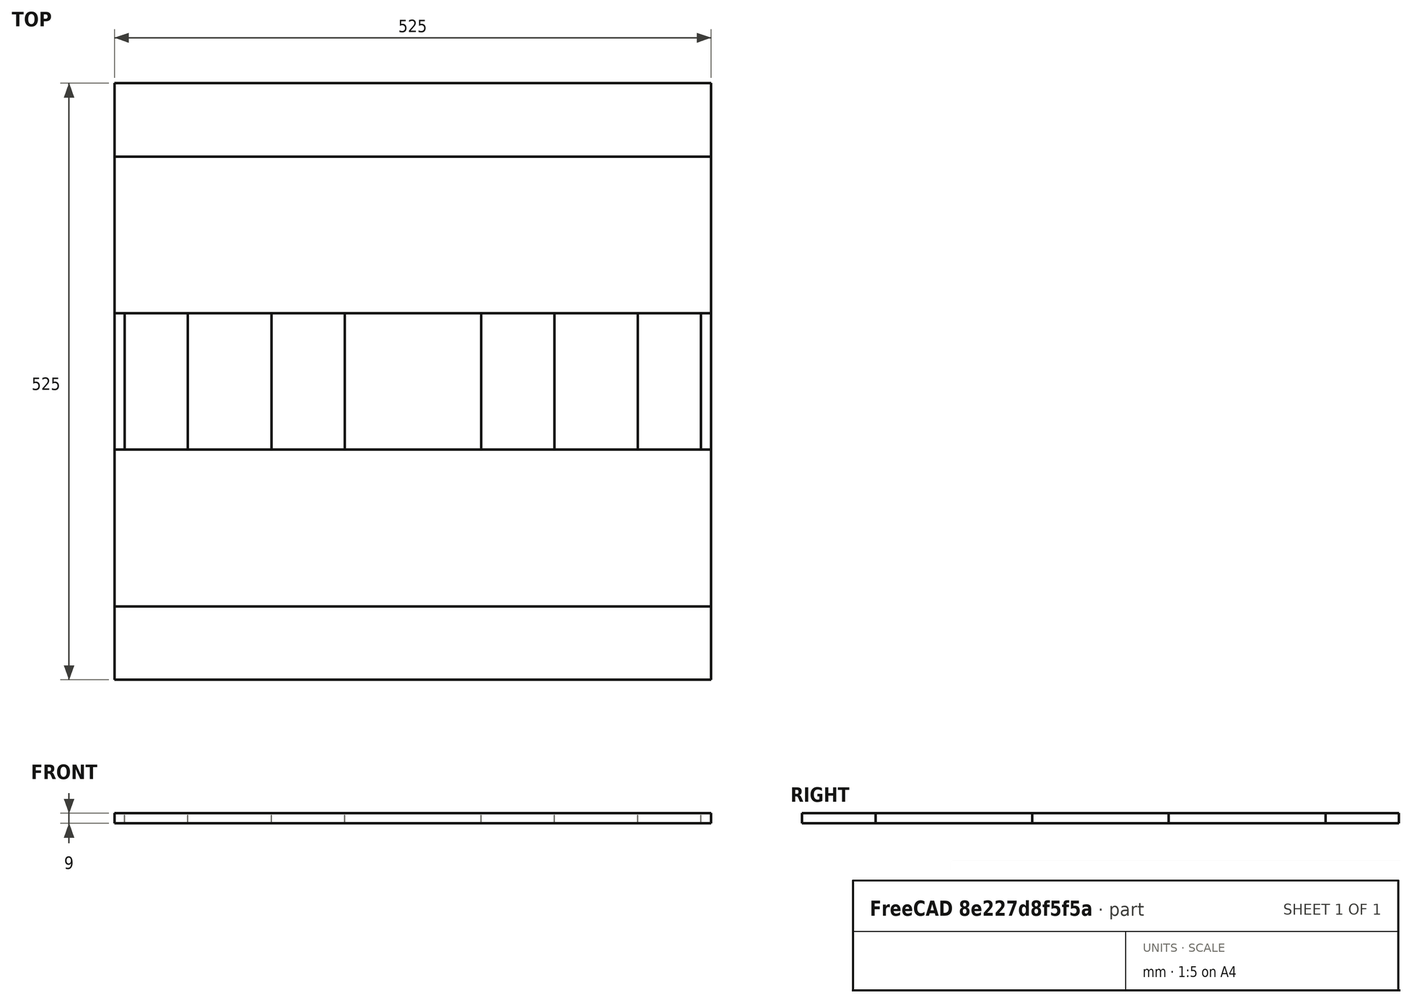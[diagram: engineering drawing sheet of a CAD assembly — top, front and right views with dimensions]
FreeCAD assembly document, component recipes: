
FREECAD ASSEMBLY — COMPONENT RECIPES ("storage-matrix")

This assembly document has 7 components, labeled P0..P6 below (a component is one placed body or linked part). 7 of them carry a construction recipe — the FreeCAD feature program that regenerates the part from scratch, quoted from this document or its linked companion documents; the rest are supplied as boundary geometry only. No exploded tour is included for this assembly.
COMPONENT P0 — recipe-attached ("BackMedium", modeled in this document).
Construction recipe (the document's own serialized feature program — sketch geometry with constraints, then the solid features built on it; lengths are millimeters unless a unit is written):

FEATURE [Sketcher::SketchObject] Sketch007
  MapMode = 5
  Support = -> [XY_Plane007]
  expr: Constraints[11] = Constraints[9] / 2
  expr: Constraints[10] = Constraints[8] / 2
  sketch-geometry (4):
    g0: LineSegment StartX=-262.5 StartY=-198 StartZ=0 EndX=262.5 EndY=-198 EndZ=0
    g1: LineSegment StartX=262.5 StartY=-198 StartZ=0 EndX=262.5 EndY=198 EndZ=0
    g2: LineSegment StartX=262.5 StartY=198 StartZ=0 EndX=-262.5 EndY=198 EndZ=0
    g3: LineSegment StartX=-262.5 StartY=198 StartZ=0 EndX=-262.5 EndY=-198 EndZ=0
  constraints (12):
    c: Coincident(g0,g1)
    c: Coincident(g1,g2)
    c: Coincident(g2,g3)
    c: Coincident(g3,g0)
    c: Horizontal(g0)
    c: Horizontal(g2)
    c: Vertical(g1)
    c: Vertical(g3)
    c: Distance(g2) = 525
    c: Distance(g1) = 396
    c: Distance(g2,g-2) = 262.5
    c: Distance(g1,g-1) = 198
FEATURE [PartDesign::Pad] Pad006
  Direction = (1,1,1)
  Length = 9
  Length2 = 100
  Profile = -> Sketch007
  Type = 0
FEATURE [PartDesign::CoordinateSystem] bottom004
  AttacherType = Attacher::AttachEngine3D
  MapMode = 5
  Placement = pos=(0,-198,0) rot=(1,0,0;1.5708rad)
  Support = -> [Pad006]
FEATURE [PartDesign::Body] BackMedium
  Group = -> [Sketch007,Pad006,bottom004]
  Origin = -> Origin007
  Tip = -> Pad006
COMPONENT P1 — recipe-attached ("back003", modeled in this document).
Construction recipe (the document's own serialized feature program — sketch geometry with constraints, then the solid features built on it; lengths are millimeters unless a unit is written):

FEATURE [PartDesign::CoordinateSystem] LCS_0002
  AttacherType = Attacher::AttachEngine3D
  MapMode = 2
  Support = -> [X_Axis005]
FEATURE [Sketcher::SketchObject] Sketch005
  MapMode = 5
  Support = -> [XY_Plane005]
  expr: Constraints[10] = Constraints[8] / 2
  expr: Constraints[11] = Constraints[9] / 2
  sketch-geometry (4):
    g0: LineSegment StartX=-262.5 StartY=-262.5 StartZ=0 EndX=262.5 EndY=-262.5 EndZ=0
    g1: LineSegment StartX=262.5 StartY=-262.5 StartZ=0 EndX=262.5 EndY=262.5 EndZ=0
    g2: LineSegment StartX=262.5 StartY=262.5 StartZ=0 EndX=-262.5 EndY=262.5 EndZ=0
    g3: LineSegment StartX=-262.5 StartY=262.5 StartZ=0 EndX=-262.5 EndY=-262.5 EndZ=0
  constraints (12):
    c: Coincident(g0,g1)
    c: Coincident(g1,g2)
    c: Coincident(g2,g3)
    c: Coincident(g3,g0)
    c: Horizontal(g0)
    c: Horizontal(g2)
    c: Vertical(g1)
    c: Vertical(g3)
    c: Distance(g2) = 525
    c: Distance(g1) = 525
    c: Distance(g2,g-2) = 262.5
    c: Distance(g1,g-1) = 262.5
FEATURE [PartDesign::Pad] Pad004
  Direction = (1,1,1)
  Length = 9
  Length2 = 100
  Profile = -> Sketch005
  Type = 0
FEATURE [PartDesign::CoordinateSystem] bottom002
  AttacherType = Attacher::AttachEngine3D
  MapMode = 5
  Placement = pos=(0,-262.5,0) rot=(1,0,0;1.5708rad)
  Support = -> [Pad004]
FEATURE [PartDesign::Body] back003
  Group = -> [LCS_0002,Sketch005,Pad004,bottom002]
  Origin = -> Origin005
  Tip = -> Pad004
COMPONENT P2 — recipe-attached ("sideMedium", modeled in this document).
Construction recipe (the document's own serialized feature program — sketch geometry with constraints, then the solid features built on it; lengths are millimeters unless a unit is written):

FEATURE [Sketcher::SketchObject] Sketch006
  MapMode = 5
  Support = -> [XY_Plane006]
  expr: Constraints[11] = Constraints[8] / 2
  expr: Constraints[10] = Constraints[9] / 2
  sketch-geometry (4):
    g0: LineSegment StartX=-198 StartY=-60 StartZ=0 EndX=198 EndY=-60 EndZ=0
    g1: LineSegment StartX=198 StartY=-60 StartZ=0 EndX=198 EndY=60 EndZ=0
    g2: LineSegment StartX=198 StartY=60 StartZ=0 EndX=-198 EndY=60 EndZ=0
    g3: LineSegment StartX=-198 StartY=60 StartZ=0 EndX=-198 EndY=-60 EndZ=0
  constraints (12):
    c: Coincident(g0,g1)
    c: Coincident(g1,g2)
    c: Coincident(g2,g3)
    c: Coincident(g3,g0)
    c: Horizontal(g0)
    c: Horizontal(g2)
    c: Vertical(g1)
    c: Vertical(g3)
    c: Distance(g2) = 396
    c: Distance(g1) = 120
    c: Distance(g2,g-1) = 60
    c: Distance(g2,g-2) = 198
FEATURE [PartDesign::Pad] Pad005
  Direction = (1,1,1)
  Length = 9
  Length2 = 100
  Profile = -> Sketch006
  Type = 0
FEATURE [PartDesign::CoordinateSystem] top003
  AttacherType = Attacher::AttachEngine3D
  MapMode = 5
  Placement = pos=(-198,0,0) rot=(0.57735,-0.57735,-0.57735;2.0944rad)
  Support = -> [Pad005]
FEATURE [PartDesign::CoordinateSystem] bottom003
  AttacherType = Attacher::AttachEngine3D
  MapMode = 5
  Placement = pos=(198,0,0) rot=(0.57735,0.57735,0.57735;2.0944rad)
  Support = -> [Pad005]
FEATURE [PartDesign::Body] sideMedium
  Group = -> [Sketch006,Pad005,top003,bottom003]
  Origin = -> Origin006
  Tip = -> Pad005
COMPONENT P3 — recipe-attached ("small", modeled in this document).
Construction recipe (the document's own serialized feature program — sketch geometry with constraints, then the solid features built on it; lengths are millimeters unless a unit is written):

FEATURE [PartDesign::CoordinateSystem] LCS_0
  AttacherType = Attacher::AttachEngine3D
  MapMode = 2
  Support = -> [X_Axis001]
FEATURE [Sketcher::SketchObject] Sketch
  MapMode = 5
  Support = -> [XY_Plane001]
  expr: Constraints[9] = Constraints[8]
  expr: Constraints[10] = Constraints[8] / 2
  expr: Constraints[11] = Constraints[8] / 2
  sketch-geometry (4):
    g0: LineSegment StartX=-60 StartY=-60 StartZ=0 EndX=60 EndY=-60 EndZ=0
    g1: LineSegment StartX=60 StartY=-60 StartZ=0 EndX=60 EndY=60 EndZ=0
    g2: LineSegment StartX=60 StartY=60 StartZ=0 EndX=-60 EndY=60 EndZ=0
    g3: LineSegment StartX=-60 StartY=60 StartZ=0 EndX=-60 EndY=-60 EndZ=0
  constraints (12):
    c: Coincident(g0,g1)
    c: Coincident(g1,g2)
    c: Coincident(g2,g3)
    c: Coincident(g3,g0)
    c: Horizontal(g0)
    c: Horizontal(g2)
    c: Vertical(g1)
    c: Vertical(g3)
    c: Distance(g2) = 120
    c: Distance(g1) = 120
    c: Distance(g2,g-1) = 60
    c: Distance(g1,g-2) = 60
FEATURE [PartDesign::Pad] Pad
  Direction = (1,1,1)
  Length = 9
  Length2 = 100
  Profile = -> Sketch
  Type = 0
FEATURE [PartDesign::CoordinateSystem] right
  AttacherType = Attacher::AttachEngine3D
  MapMode = 5
  Placement = pos=(0,0,9) rot=(0,0,1;0rad)
  Support = -> [Pad]
FEATURE [PartDesign::Body] small
  Group = -> [LCS_0,Sketch,Pad,right]
  Origin = -> Origin001
  Tip = -> Pad
COMPONENT P4 — recipe-attached ("horizontalLarge", modeled in this document).
Construction recipe (the document's own serialized feature program — sketch geometry with constraints, then the solid features built on it; lengths are millimeters unless a unit is written):

FEATURE [PartDesign::CoordinateSystem] LCS_0001
  AttacherType = Attacher::AttachEngine3D
  MapMode = 2
  Support = -> [X_Axis002]
FEATURE [Sketcher::SketchObject] Sketch001
  MapMode = 5
  Support = -> [XY_Plane002]
  expr: Constraints[10] = Constraints[8] / 2
  expr: Constraints[11] = Constraints[9] / 2
  sketch-geometry (4):
    g0: LineSegment StartX=-253.5 StartY=-60 StartZ=0 EndX=253.5 EndY=-60 EndZ=0
    g1: LineSegment StartX=253.5 StartY=-60 StartZ=0 EndX=253.5 EndY=60 EndZ=0
    g2: LineSegment StartX=253.5 StartY=60 StartZ=0 EndX=-253.5 EndY=60 EndZ=0
    g3: LineSegment StartX=-253.5 StartY=60 StartZ=0 EndX=-253.5 EndY=-60 EndZ=0
  constraints (12):
    c: Coincident(g0,g1)
    c: Coincident(g1,g2)
    c: Coincident(g2,g3)
    c: Coincident(g3,g0)
    c: Horizontal(g0)
    c: Horizontal(g2)
    c: Vertical(g1)
    c: Vertical(g3)
    c: Distance(g2) = 507
    c: Distance(g1) = 120
    c: Distance(g2,g-2) = 253.5
    c: Distance(g1,g-1) = 60
FEATURE [PartDesign::Pad] Pad001
  Direction = (1,1,1)
  Length = 9
  Length2 = 100
  Profile = -> Sketch001
  Type = 0
FEATURE [PartDesign::CoordinateSystem] top
  AttacherType = Attacher::AttachEngine3D
  MapMode = 5
  Placement = pos=(0,0,9) rot=(0,0,1;0rad)
  Support = -> [Pad001]
FEATURE [PartDesign::CoordinateSystem] left
  AttacherType = Attacher::AttachEngine3D
  MapMode = 5
  Placement = pos=(-253.5,0,0) rot=(0.57735,-0.57735,-0.57735;2.0944rad)
  Support = -> [Pad001]
FEATURE [PartDesign::CoordinateSystem] right001
  AttacherType = Attacher::AttachEngine3D
  MapMode = 5
  Placement = pos=(253.5,0,0) rot=(0.57735,0.57735,0.57735;2.0944rad)
  Support = -> [Pad001]
FEATURE [PartDesign::CoordinateSystem] back
  AttacherType = Attacher::AttachEngine3D
  MapMode = 5
  Placement = pos=(0,60,0) rot=(0,0.707107,0.707107;3.14159rad)
  Support = -> [Pad001]
FEATURE [PartDesign::Body] verticalLarge  label="horizontalLarge"
  Group = -> [LCS_0001,Sketch001,Pad001,top,left,right001,back]
  Origin = -> Origin002
  Tip = -> Pad001
COMPONENT P5 — recipe-attached ("verticalLarge003", modeled in this document).
Construction recipe (the document's own serialized feature program — sketch geometry with constraints, then the solid features built on it; lengths are millimeters unless a unit is written):

FEATURE [Sketcher::SketchObject] Sketch004
  MapMode = 5
  Support = -> [XY_Plane004]
  expr: Constraints[10] = Constraints[8] / 2
  expr: Constraints[11] = Constraints[9] / 2
  sketch-geometry (4):
    g0: LineSegment StartX=-262.5 StartY=-60 StartZ=0 EndX=262.5 EndY=-60 EndZ=0
    g1: LineSegment StartX=262.5 StartY=-60 StartZ=0 EndX=262.5 EndY=60 EndZ=0
    g2: LineSegment StartX=262.5 StartY=60 StartZ=0 EndX=-262.5 EndY=60 EndZ=0
    g3: LineSegment StartX=-262.5 StartY=60 StartZ=0 EndX=-262.5 EndY=-60 EndZ=0
  constraints (12):
    c: Coincident(g0,g1)
    c: Coincident(g1,g2)
    c: Coincident(g2,g3)
    c: Coincident(g3,g0)
    c: Horizontal(g0)
    c: Horizontal(g2)
    c: Vertical(g1)
    c: Vertical(g3)
    c: Distance(g2) = 525
    c: Distance(g1) = 120
    c: Distance(g2,g-2) = 262.5
    c: Distance(g1,g-1) = 60
FEATURE [PartDesign::Pad] Pad003
  Direction = (1,1,1)
  Length = 9
  Length2 = 100
  Profile = -> Sketch004
  Type = 0
FEATURE [PartDesign::CoordinateSystem] top002
  AttacherType = Attacher::AttachEngine3D
  MapMode = 5
  Placement = pos=(-262.5,0,0) rot=(0.57735,-0.57735,-0.57735;2.0944rad)
  Support = -> [Pad003]
FEATURE [PartDesign::CoordinateSystem] bottom001
  AttacherType = Attacher::AttachEngine3D
  MapMode = 5
  Placement = pos=(262.5,0,0) rot=(0.57735,0.57735,0.57735;2.0944rad)
  Support = -> [Pad003]
FEATURE [PartDesign::CoordinateSystem] left002
  AttacherType = Attacher::AttachEngine3D
  MapMode = 5
  Placement = pos=(0,0,0) rot=(1,0,0;3.14159rad)
  Support = -> [Pad003]
FEATURE [PartDesign::CoordinateSystem] right003
  AttacherType = Attacher::AttachEngine3D
  MapMode = 5
  Placement = pos=(0,0,9) rot=(0,0,1;0rad)
  Support = -> [Pad003]
FEATURE [PartDesign::CoordinateSystem] front001
  AttacherType = Attacher::AttachEngine3D
  MapMode = 5
  Placement = pos=(0,-60,0) rot=(1,0,0;1.5708rad)
  Support = -> [Pad003]
FEATURE [PartDesign::CoordinateSystem] back002
  AttacherType = Attacher::AttachEngine3D
  Support = -> [Pad003]
FEATURE [PartDesign::Body] verticalLarge003
  Group = -> [Sketch004,Pad003,top002,bottom001,left002,right003,front001,back002]
  Origin = -> Origin004
  Tip = -> Pad003
COMPONENT P6 — recipe-attached ("verticalMedium", modeled in this document).
Construction recipe (the document's own serialized feature program — sketch geometry with constraints, then the solid features built on it; lengths are millimeters unless a unit is written):

FEATURE [Sketcher::SketchObject] Sketch002
  MapMode = 5
  Support = -> [XY_Plane003]
  expr: Constraints[10] = Constraints[8] / 2
  expr: Constraints[11] = Constraints[9] / 2
  sketch-geometry (4):
    g0: LineSegment StartX=-124.5 StartY=-60 StartZ=0 EndX=124.5 EndY=-60 EndZ=0
    g1: LineSegment StartX=124.5 StartY=-60 StartZ=0 EndX=124.5 EndY=60 EndZ=0
    g2: LineSegment StartX=124.5 StartY=60 StartZ=0 EndX=-124.5 EndY=60 EndZ=0
    g3: LineSegment StartX=-124.5 StartY=60 StartZ=0 EndX=-124.5 EndY=-60 EndZ=0
  constraints (12):
    c: Coincident(g0,g1)
    c: Coincident(g1,g2)
    c: Coincident(g2,g3)
    c: Coincident(g3,g0)
    c: Horizontal(g0)
    c: Horizontal(g2)
    c: Vertical(g1)
    c: Vertical(g3)
    c: Distance(g2) = 249
    c: Distance(g1) = 120
    c: Distance(g2,g-2) = 124.5
    c: Distance(g1,g-1) = 60
FEATURE [PartDesign::Pad] Pad002
  Direction = (1,1,1)
  Length = 9
  Length2 = 100
  Profile = -> Sketch002
  Type = 0
FEATURE [PartDesign::CoordinateSystem] top001
  AttacherType = Attacher::AttachEngine3D
  MapMode = 5
  Placement = pos=(0,0,9) rot=(0,0,1;0rad)
  Support = -> [Pad002]
FEATURE [PartDesign::CoordinateSystem] bottom
  AttacherType = Attacher::AttachEngine3D
  MapMode = 5
  Placement = pos=(0,0,0) rot=(1,0,0;3.14159rad)
  Support = -> [Pad002]
FEATURE [PartDesign::CoordinateSystem] left001
  AttacherType = Attacher::AttachEngine3D
  MapMode = 5
  Placement = pos=(-124.5,0,0) rot=(0.57735,-0.57735,-0.57735;2.0944rad)
  Support = -> [Pad002]
FEATURE [PartDesign::CoordinateSystem] right002
  AttacherType = Attacher::AttachEngine3D
  MapMode = 5
  Placement = pos=(124.5,0,0) rot=(0.57735,0.57735,0.57735;2.0944rad)
  Support = -> [Pad002]
FEATURE [PartDesign::CoordinateSystem] front
  AttacherType = Attacher::AttachEngine3D
  MapMode = 5
  Placement = pos=(0,-60,0) rot=(1,0,0;1.5708rad)
  Support = -> [Pad002]
FEATURE [PartDesign::CoordinateSystem] back001
  AttacherType = Attacher::AttachEngine3D
  MapMode = 5
  Placement = pos=(0,60,0) rot=(0,0.707107,0.707107;3.14159rad)
  Support = -> [Pad002]
FEATURE [Sketcher::SketchObject] Sketch003
  MapMode = 5
  Support = -> [XY_Plane003]
FEATURE [PartDesign::Body] verticalMedium
  Group = -> [Sketch002,Pad002,top001,bottom,left001,right002,front,back001,Sketch003]
  Origin = -> Origin003
  Tip = -> Pad002
PROVENANCE & LICENSES
A FreeCAD (.FCStd) document from a public repository crawl; recipes are the document's own serialized feature recipes (and, for linked parts, companion documents' recipes).
License: as declared in the source repository (recorded in the dataset sidecar).
